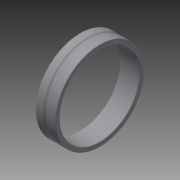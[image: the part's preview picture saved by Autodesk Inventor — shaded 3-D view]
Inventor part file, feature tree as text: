
AUTODESK INVENTOR PART (.ipt)
format: ipt  version: 2014 SP2 (Build 180246200, 246)  size: 157,696 bytes
history: native  units: mm
features: other x14, revolve x1, sketch x1
ambient origin geometry x8: Origin, YZ Plane, XZ Plane, XY Plane, X Axis, Y Axis, Z Axis, Center Point
bodies: Solid1 (feature_tree)
feature tree (16):
  revolve  "Revolution1"  [1 undecoded]
  other  "1_XY"
  other  "1_YZ"
  other  "1_ZX"
  other  "1_X"
  other  "1_Y"
  other  "1_Z"
  other  "1_Center"
  other  "1_Dummy_XY"
  other  "1_Dummy_YZ"
  other  "1_Dummy_ZX"
  other  "1_Dummy_X"
  other  "1_Dummy_Y"
  other  "1_Dummy_Z"
  other  "1_Dummy_Center"
  sketch  "Sketch_1"  dims[d0=360.0deg d1=0.0mm]
note: 1 required parameter value undecoded (feature->parameter linkage not recoverable at this tier; creation-order binding heuristic only, values carry confidence <= 0.55)
